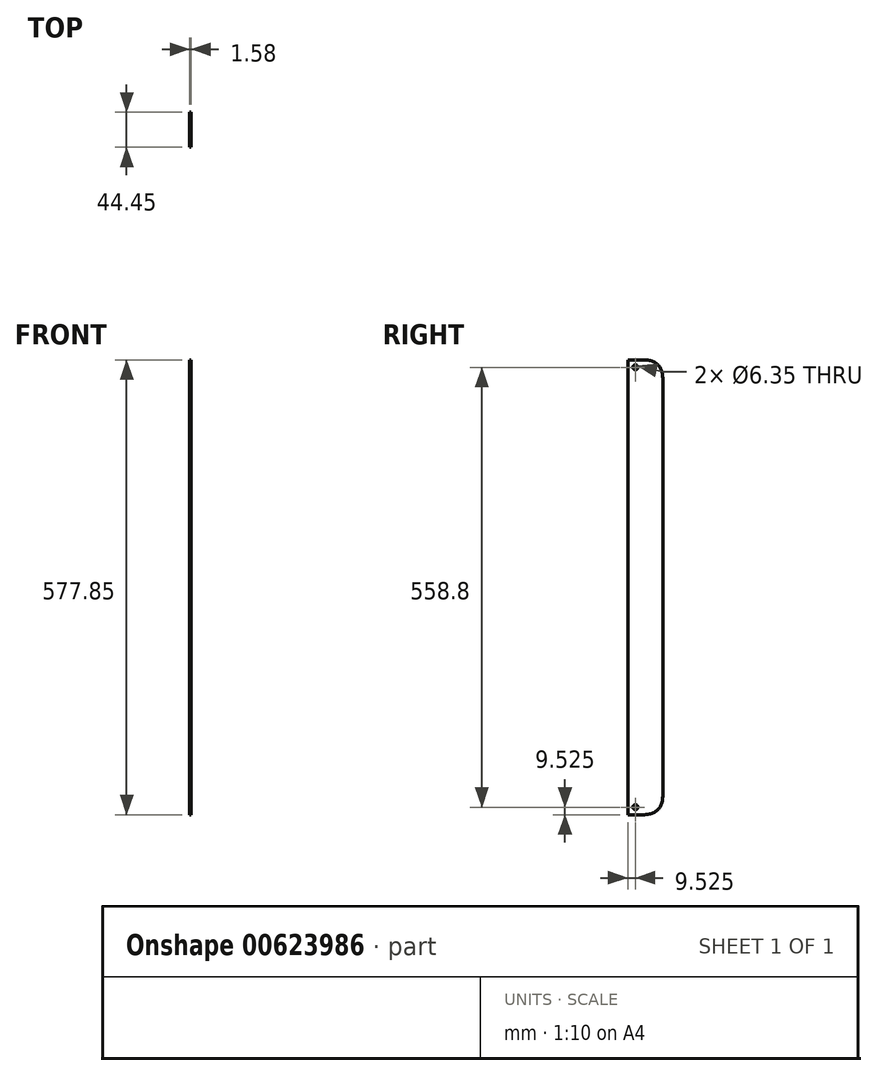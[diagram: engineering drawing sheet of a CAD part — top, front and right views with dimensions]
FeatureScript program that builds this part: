
annotation { "Feature Type Name" : "Feature", "Feature Type Description" : "" }
export const myFeature = defineFeature(function(context is Context, id is Id, definition is map)
    precondition{}
    {
        {
            var Q0;
            Q0=qCreatedBy(makeId("Top.planeOp"),FACE);
            var sketch = newSketch(context, id + "F0", { "sketchPlane" : qUnion([Q0])});
            skLineSegment(sketch, "E0.bottom", {"start": v(-54.45, 41.1) * mm, "end": v(-52.87, 41.1) * mm});
            skLineSegment(sketch, "E0.top", {"start": v(-54.45, -3.36) * mm, "end": v(-52.87, -3.36) * mm});
            skLineSegment(sketch, "E0.left", {"start": v(-54.45, 41.1) * mm, "end": v(-54.45, -3.36) * mm});
            skLineSegment(sketch, "E0.right", {"start": v(-52.87, 41.1) * mm, "end": v(-52.87, -3.36) * mm});
            skSolve(sketch);
        }
        {
            var Q0;
            Q0=makeQuery(id+"F0.imprint","IMPRINT",FACE,{"disambiguationData":[TD([[makeQuery(id+"F0.imprint","IMPRINT",EDGE,{"derivedFrom":sQuery(id+"F0.wireOp",EDGE,"E0.bottom")}),-1.0]])]});
            extrude(context, id + "F1", {"entities" : qUnion([Q0]), "depth" : 577.85 * mm, "offsetDistance" : 25.4 * mm});
        }
        {
            var Q0;
            Q0=makeQuery(id+"F1.opExtrude","SWEPT_FACE",FACE,{"disambiguationData":[OSD([sQuery(id+"F0.wireOp",EDGE,"E0.left")])]});
            var sketch = newSketch(context, id + "F2", { "sketchPlane" : qUnion([Q0])});
            skCircle(sketch, "E1", {"center": v(-6.17, 568.33) * mm, "radius": 3.18 * mm});
            skCircle(sketch, "E2", {"center": v(-6.17, 9.53) * mm, "radius": 3.18 * mm});
            skSolve(sketch);
        }
        {
            var Q0;
            Q0=makeQuery(id+"F2.imprint","IMPRINT",FACE,{"disambiguationData":[TD([[makeQuery(id+"F2.imprint","IMPRINT",EDGE,{"derivedFrom":sQuery(id+"F2.wireOp",EDGE,"E2")}),1.0]])]});
            var Q1;
            Q1=makeQuery(id+"F2.imprint","IMPRINT",FACE,{"disambiguationData":[TD([[makeQuery(id+"F2.imprint","IMPRINT",EDGE,{"derivedFrom":sQuery(id+"F2.wireOp",EDGE,"E1")}),1.0]])]});
            extrude(context, id + "F3", {"entities" : qUnion([Q0, Q1]), "operationType" : NewBodyOperationType.REMOVE, "oppositeDirection" : true, "depth" : 1.59 * mm, "offsetDistance" : 25.4 * mm});
        }
        {
            var Q0;
            Q0=makeQuery(id+"F1.opExtrude","CAP_EDGE",EDGE,{"disambiguationData":[OSD([sQuery(id+"F0.wireOp",EDGE,"E0.bottom")])],"isStart":false});
            var Q1;
            Q1=makeQuery(id+"F1.opExtrude","CAP_EDGE",EDGE,{"disambiguationData":[OSD([sQuery(id+"F0.wireOp",EDGE,"E0.bottom")])],"isStart":true});
            fillet(context, id + "F4", {"entities" : qUnion([Q0, Q1]), "radius" : 25.4 * mm, "tangentPropagation" : true, "rho" : 0.5, "crossSection" : FilletCrossSection.CONIC, "allowEdgeOverflow" : false});
        }
    });
